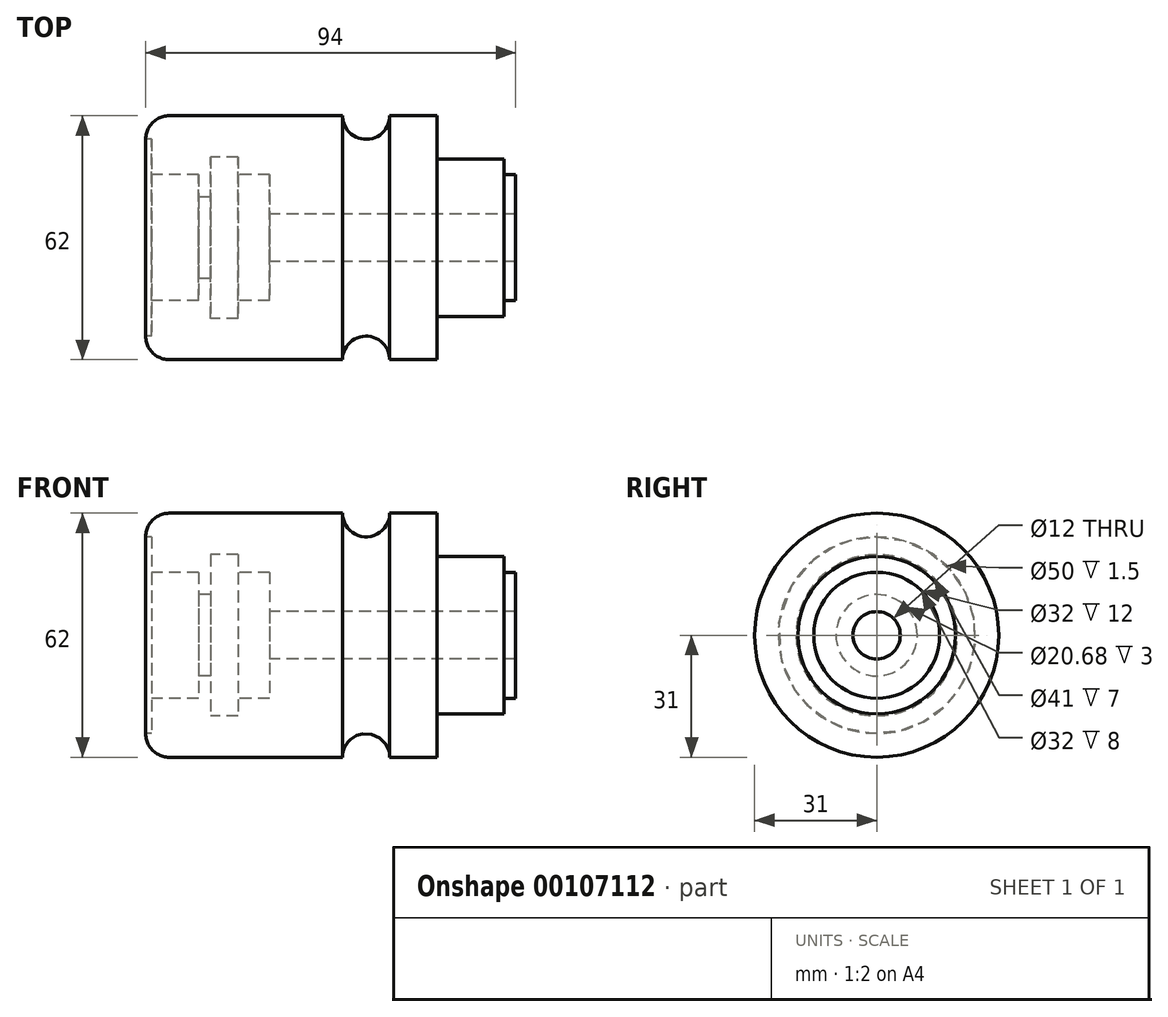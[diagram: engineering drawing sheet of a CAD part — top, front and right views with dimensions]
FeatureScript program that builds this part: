
annotation { "Feature Type Name" : "Feature", "Feature Type Description" : "" }
export const myFeature = defineFeature(function(context is Context, id is Id, definition is map)
    precondition{}
    {
        {
            var Q0;
            Q0=qCreatedBy(makeId("Front.planeOp"),FACE);
            var sketch = newSketch(context, id + "F0", { "sketchPlane" : qUnion([Q0])});
            skLineSegment(sketch, "E0", {"start": v(0, 25) * mm, "end": v(0, -23.44) * mm});
            skLineSegment(sketch, "E1", {"start": v(-53.3, 0) * mm, "end": v(292.34, 0) * mm, "construction": true});
            skArc(sketch, "E2", {"start": v(62, -29.44) * mm, "mid": v(56, -23.44) * mm, "end": v(50, -29.44) * mm});
            skLineSegment(sketch, "E3", {"start": v(6, 31) * mm, "end": v(50, 31) * mm});
            skArc(sketch, "E4", {"start": v(50, 31) * mm, "mid": v(56, 25) * mm, "end": v(62, 31) * mm});
            skLineSegment(sketch, "E5", {"start": v(62, 31) * mm, "end": v(74, 31) * mm});
            skLineSegment(sketch, "E6", {"start": v(62, -29.44) * mm, "end": v(74, -29.44) * mm});
            skLineSegment(sketch, "E7", {"start": v(74, 31) * mm, "end": v(74, -29.44) * mm});
            skLineSegment(sketch, "E8", {"start": v(74, 20) * mm, "end": v(91, 20) * mm});
            skLineSegment(sketch, "E9", {"start": v(91, 20) * mm, "end": v(91, -19.26) * mm});
            skLineSegment(sketch, "E10", {"start": v(91, -19.26) * mm, "end": v(74, -19.26) * mm});
            skLineSegment(sketch, "E11", {"start": v(74, -19.26) * mm, "end": v(74, 20) * mm});
            skLineSegment(sketch, "E12.bottom", {"start": v(91, 16) * mm, "end": v(94, 16) * mm});
            skLineSegment(sketch, "E12.top", {"start": v(91, -13.67) * mm, "end": v(94, -13.67) * mm});
            skLineSegment(sketch, "E12.left", {"start": v(91, 16) * mm, "end": v(91, -13.67) * mm});
            skLineSegment(sketch, "E12.right", {"start": v(94, 16) * mm, "end": v(94, -13.67) * mm});
            skLineSegment(sketch, "E13", {"start": v(50, -29.44) * mm, "end": v(6, -29.44) * mm});
            skArc(sketch, "E14", {"start": v(0, -23.44) * mm, "mid": v(1.76, -27.68) * mm, "end": v(6, -29.44) * mm});
            skArc(sketch, "E15", {"start": v(0, 25) * mm, "mid": v(1.76, 29.24) * mm, "end": v(6, 31) * mm});
            skLineSegment(sketch, "E16", {"start": v(0, 25) * mm, "end": v(1.5, 25) * mm, "construction": true});
            skLineSegment(sketch, "E17", {"start": v(1.5, 25) * mm, "end": v(1.5, -23.44) * mm});
            skLineSegment(sketch, "E18", {"start": v(1.5, -23.44) * mm, "end": v(0, -23.44) * mm, "construction": true});
            skLineSegment(sketch, "E19", {"start": v(1.5, 16) * mm, "end": v(13.5, 16) * mm});
            skLineSegment(sketch, "E20", {"start": v(13.5, 16) * mm, "end": v(13.5, -16) * mm});
            skLineSegment(sketch, "E21", {"start": v(13.5, -16) * mm, "end": v(0, -16) * mm});
            skLineSegment(sketch, "E22", {"start": v(13.5, 10.34) * mm, "end": v(16.5, 10.34) * mm});
            skLineSegment(sketch, "E23", {"start": v(16.5, 10.34) * mm, "end": v(16.5, -9.23) * mm});
            skLineSegment(sketch, "E24", {"start": v(16.5, -9.23) * mm, "end": v(13.5, -9.23) * mm});
            skLineSegment(sketch, "E25", {"start": v(16.5, 10.34) * mm, "end": v(16.5, 20.5) * mm});
            skLineSegment(sketch, "E26", {"start": v(16.5, 20.5) * mm, "end": v(23.5, 20.5) * mm});
            skLineSegment(sketch, "E27", {"start": v(23.5, 20.5) * mm, "end": v(23.5, -19.4) * mm});
            skLineSegment(sketch, "E28", {"start": v(23.5, -19.4) * mm, "end": v(16.5, -19.4) * mm});
            skLineSegment(sketch, "E29", {"start": v(16.5, -19.4) * mm, "end": v(16.5, -9.23) * mm});
            skLineSegment(sketch, "E30", {"start": v(23.5, 16) * mm, "end": v(31.5, 16) * mm});
            skLineSegment(sketch, "E31", {"start": v(31.5, 16) * mm, "end": v(31.5, -16) * mm});
            skLineSegment(sketch, "E32", {"start": v(31.5, -16) * mm, "end": v(23.5, -16) * mm});
            skLineSegment(sketch, "E33", {"start": v(31.5, 6) * mm, "end": v(94, 6) * mm});
            skLineSegment(sketch, "E34", {"start": v(31.5, -6) * mm, "end": v(94, -6) * mm});
            skLineSegment(sketch, "E35", {"start": v(62, 31) * mm, "end": v(62, -29.44) * mm});
            skLineSegment(sketch, "E36", {"start": v(50, 31) * mm, "end": v(50, -29.44) * mm});
            skLineSegment(sketch, "E37", {"start": v(0, 25) * mm, "end": v(1.5, 25) * mm});
            skLineSegment(sketch, "E38", {"start": v(0, -23.44) * mm, "end": v(1.5, -23.44) * mm});
            skSolve(sketch);
        }
        {
            var Q0;
            {var subQ4=sQuery(id+"F0.wireOp",EDGE,"E3");Q0=makeQuery(id+"F0.imprint","IMPRINT",FACE,{"disambiguationData":[TD([[makeQuery(id+"F0.imprint","IMPRINT",EDGE,{"derivedFrom":subQ4}),-1.0]])]});}
            var Q1;
            {var subQ0=sQuery(id+"F0.wireOp",EDGE,"E4");Q1=makeQuery(id+"F0.imprint","IMPRINT",FACE,{"disambiguationData":[TD([[makeQuery(id+"F0.imprint","IMPRINT",EDGE,{"derivedFrom":subQ0}),-1.0]])]});}
            var Q2;
            {var subQ7=sQuery(id+"F0.wireOp",EDGE,"E5");Q2=makeQuery(id+"F0.imprint","IMPRINT",FACE,{"disambiguationData":[TD([[makeQuery(id+"F0.imprint","IMPRINT",EDGE,{"derivedFrom":subQ7}),-1.0]])]});}
            var Q3;
            {var subQ6=sQuery(id+"F0.wireOp",EDGE,"E8");Q3=makeQuery(id+"F0.imprint","IMPRINT",FACE,{"disambiguationData":[TD([[makeQuery(id+"F0.imprint","IMPRINT",EDGE,{"derivedFrom":subQ6}),-1.0]])]});}
            var Q4;
            {var subQ0=sQuery(id+"F0.wireOp",EDGE,"E12.bottom");Q4=makeQuery(id+"F0.imprint","IMPRINT",FACE,{"disambiguationData":[TD([[makeQuery(id+"F0.imprint","IMPRINT",EDGE,{"derivedFrom":subQ0}),-1.0]])]});}
            var Q5;
            Q5=sQuery(id+"F0.wireOp",EDGE,"E1");
            revolve(context, id + "F1", {"entities" : qUnion([Q0, Q1, Q2, Q3, Q4]), "axis" : qUnion([Q5]), "revolveType" : RevolveType.FULL});
        }
    });
